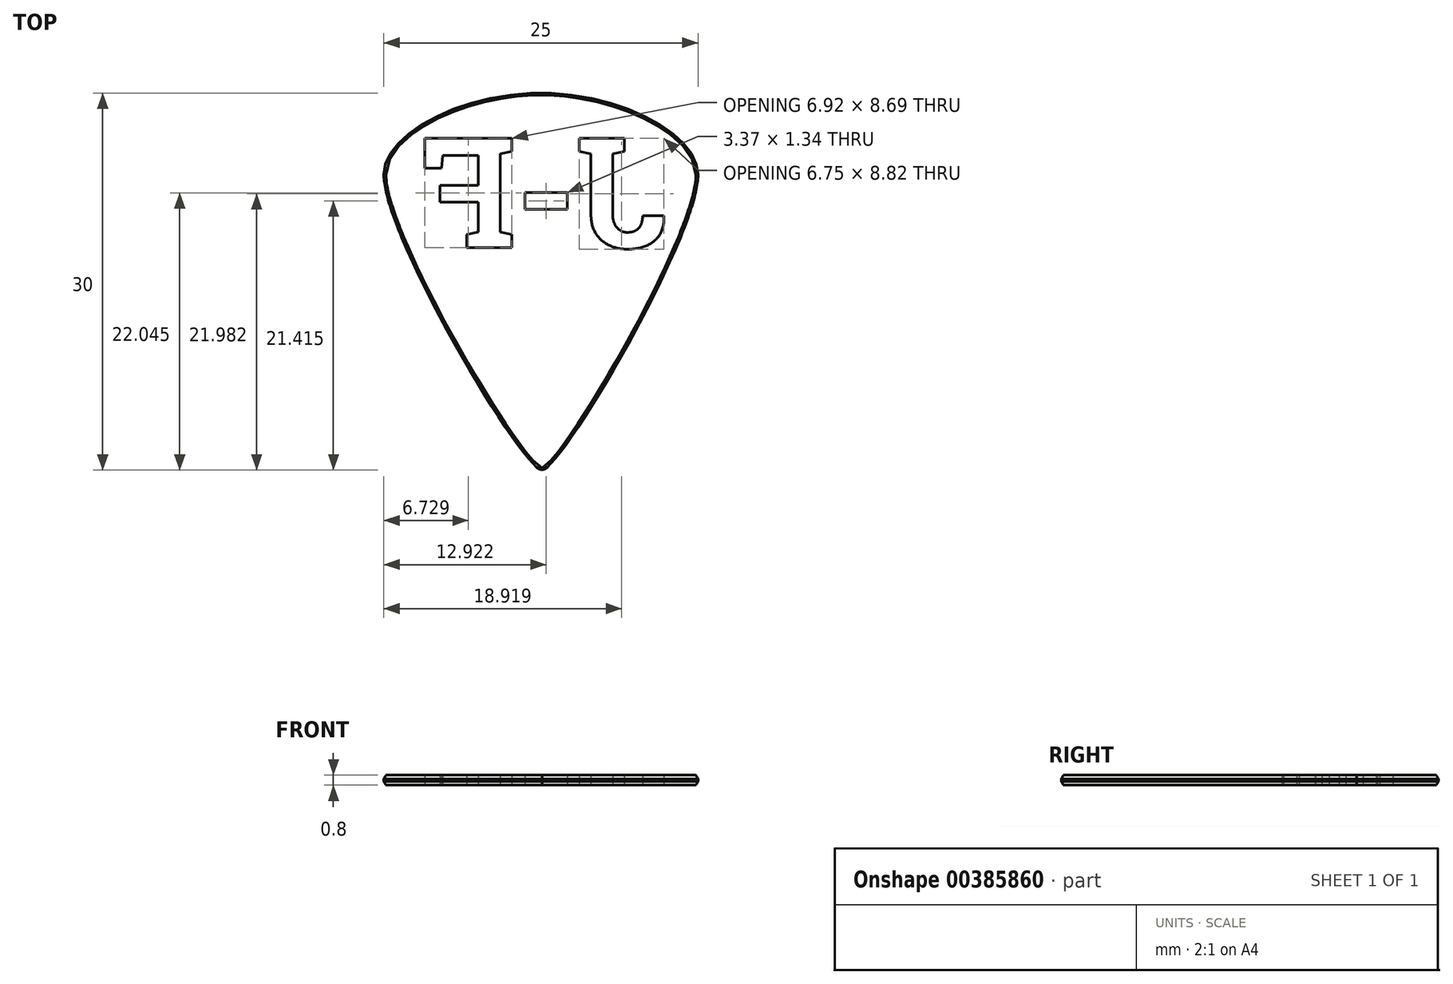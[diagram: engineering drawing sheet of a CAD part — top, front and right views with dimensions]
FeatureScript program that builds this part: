
annotation { "Feature Type Name" : "Feature", "Feature Type Description" : "" }
export const myFeature = defineFeature(function(context is Context, id is Id, definition is map)
    precondition{}
    {
        {
            var Q0;
            Q0=qCreatedBy(makeId("Top.planeOp"),FACE);
            var sketch = newSketch(context, id + "F0", { "sketchPlane" : qUnion([Q0])});
            skLineSegment(sketch, "E0", {"start": v(0.08, -23.5) * mm, "end": v(12.5, 0) * mm, "construction": true});
            skLineSegment(sketch, "E1", {"start": v(12.5, 0) * mm, "end": v(0, 6.5) * mm, "construction": true});
            skLineSegment(sketch, "E2", {"start": v(0, 6.5) * mm, "end": v(-12.5, 0) * mm, "construction": true});
            skLineSegment(sketch, "E3", {"start": v(0.08, -23.5) * mm, "end": v(-12.5, 0) * mm, "construction": true});
            skLineSegment(sketch, "E4", {"start": v(12.5, 0) * mm, "end": v(12.5, 6.5) * mm, "construction": true});
            skLineSegment(sketch, "E5", {"start": v(0, 0) * mm, "end": v(0, 6.5) * mm, "construction": true});
            skLineSegment(sketch, "E6", {"start": v(0, 0) * mm, "end": v(0.08, -23.5) * mm, "construction": true});
            skLineSegment(sketch, "E7", {"start": v(-12.5, 0) * mm, "end": v(-12.57, 6.5) * mm, "construction": true});
            skLineSegment(sketch, "E8", {"start": v(0, 0) * mm, "end": v(-12.5, 0) * mm, "construction": true});
            skFitSpline(sketch, "E9", {"points": [v(-12.5, 0) * mm, v(0, 6.5) * mm, v(12.5, 0) * mm], "startDerivative": vector(-0.2, 19.5) * mm, "endDerivative": vector(0, -19.5) * mm});
            skLineSegment(sketch, "E10", {"start": v(-12.5, 0) * mm, "end": v(-12.5, -23.5) * mm, "construction": true});
            skLineSegment(sketch, "E11", {"start": v(0.08, -23.5) * mm, "end": v(-12.5, -23.5) * mm, "construction": true});
            skLineSegment(sketch, "E12", {"start": v(0.08, -23.5) * mm, "end": v(12.5, -23.5) * mm, "construction": true});
            skLineSegment(sketch, "E13", {"start": v(12.5, 0) * mm, "end": v(12.5, -23.5) * mm, "construction": true});
            skLineSegment(sketch, "E14", {"start": v(-12.5, -5) * mm, "end": v(12.5, -5) * mm});
            skLineSegment(sketch, "E15", {"start": v(0, 0) * mm, "end": v(12.5, 0) * mm, "construction": true});
            skLineSegment(sketch, "E16", {"start": v(1.58, -23.5) * mm, "end": v(1.58, -21.65) * mm, "construction": true});
            skFitSpline(sketch, "E17", {"points": [v(12.5, 0) * mm, v(0.08, -23.5) * mm], "startDerivative": vector(0, -15) * mm, "endDerivative": vector(-4.5, 0) * mm});
            skLineSegment(sketch, "E18", {"start": v(-1.42, -23.5) * mm, "end": v(-1.42, -21.37) * mm, "construction": true});
            skFitSpline(sketch, "E19", {"points": [v(-12.5, 0) * mm, v(0.08, -23.5) * mm], "startDerivative": vector(0, -15) * mm, "endDerivative": vector(4.5, 0) * mm});
            skSolve(sketch);
        }
        {
            var Q0;
            Q0=qSketchRegion(id+"F0",true);
            extrude(context, id + "F1", {"entities" : qUnion([Q0]), "depth" : 0.3 * mm, "hasSecondDirection" : true, "secondDirectionOppositeDirection" : true, "secondDirectionDepth" : 0.5 * mm});
        }
        {
            var Q0;
            Q0=makeQuery(id+"F1.opExtrude","CAP_FACE",FACE,{"disambiguationData":[OSD([sQuery(id+"F0.wireOp",EDGE,"E9"),sQuery(id+"F0.wireOp",EDGE,"E17"),sQuery(id+"F0.wireOp",EDGE,"E19")])],"isStart":false});
            var sketch = newSketch(context, id + "F2", { "sketchPlane" : qUnion([Q0])});
            skText(sketch, "E20", { "text": "J-F", "fontName": "RobotoSlab-Bold.ttf"});
            const initialGuessF2  = {"E20": [-0.01, -0.0058, 1, 0, 0.0088]};
            skSetInitialGuess(sketch, initialGuessF2);
            skSolve(sketch);
        }
        {
            var Q0;
            Q0=makeQuery(id+"F1.opExtrude","CAP_EDGE",EDGE,{"disambiguationData":[OSD([sQuery(id+"F0.wireOp",EDGE,"E9")])],"isStart":false});
            var Q1;
            Q1=makeQuery(id+"F1.opExtrude","CAP_EDGE",EDGE,{"disambiguationData":[OSD([sQuery(id+"F0.wireOp",EDGE,"E9")])],"isStart":true});
            chamfer(context, id + "F3", {"entities" : qUnion([Q0, Q1]), "chamferType" : ChamferType.OFFSET_ANGLE, "width" : 0.3 * mm, "oppositeDirection" : false, "angle" : 30 * degree, "tangentPropagation" : true});
        }
        {
            var Q0;
            Q0=makeQuery(id+"F1.opExtrude","CAP_FACE",FACE,{"disambiguationData":[OSD([sQuery(id+"F0.wireOp",EDGE,"E9"),sQuery(id+"F0.wireOp",EDGE,"E17"),sQuery(id+"F0.wireOp",EDGE,"E19")])],"isStart":true});
            var sketch = newSketch(context, id + "F4", { "sketchPlane" : qUnion([Q0])});
            skText(sketch, "E21", { "text": "J-F", "fontName": "RobotoSlab-Bold.ttf"});
            const initialGuessF4  = {"E21": [0.01, 0.0058, -1, 0, 0.0088]};
            skSetInitialGuess(sketch, initialGuessF4);
            skSolve(sketch);
        }
        {
            var Q0;
            Q0=qSketchRegion(id+"F4",true);
            extrude(context, id + "F5", {"entities" : qUnion([Q0]), "operationType" : NewBodyOperationType.REMOVE, "endBound" : BoundingType.UP_TO_NEXT, "oppositeDirection" : true, "depth" : 0.2 * mm});
        }
    });
